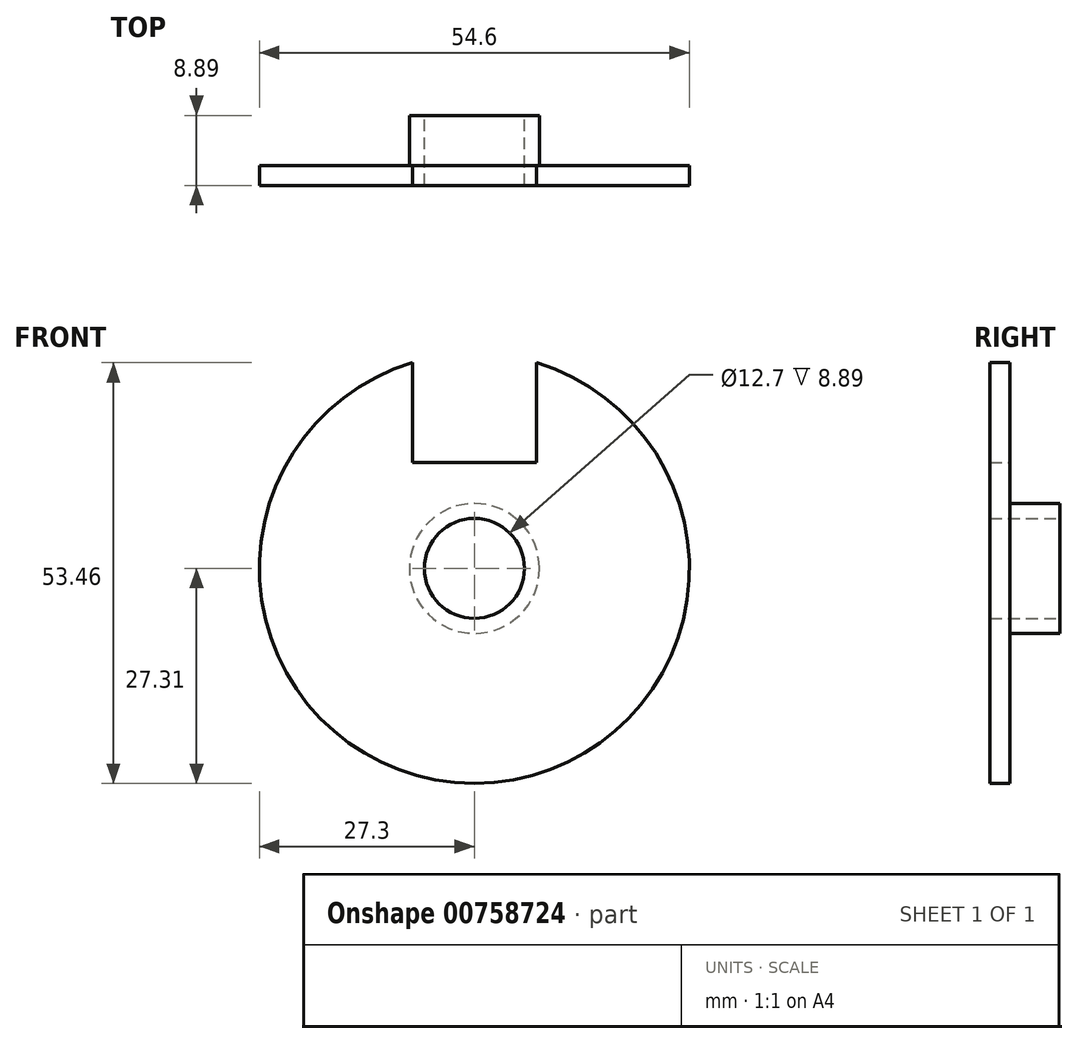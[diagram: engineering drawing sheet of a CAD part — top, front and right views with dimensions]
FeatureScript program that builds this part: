
annotation { "Feature Type Name" : "Feature", "Feature Type Description" : "" }
export const myFeature = defineFeature(function(context is Context, id is Id, definition is map)
    precondition{}
    {
        {
            var Q0;
            Q0=qCreatedBy(makeId("Front.planeOp"),FACE);
            var sketch = newSketch(context, id + "F0", { "sketchPlane" : qUnion([Q0])});
            skCircle(sketch, "E0", {"center": v(0, 0) * mm, "radius": 27.3 * mm});
            skCircle(sketch, "E1", {"center": v(0, 0) * mm, "radius": 6.35 * mm});
            skCircle(sketch, "E2", {"center": v(0, 0) * mm, "radius": 8.26 * mm});
            skLineSegment(sketch, "E3", {"start": v(0, 0) * mm, "end": v(0, 21.08) * mm});
            skCircle(sketch, "E4", {"center": v(0, 21.08) * mm, "radius": 7.62 * mm});
            skLineSegment(sketch, "E5", {"start": v(0, 21.08) * mm, "end": v(0, 13.46) * mm});
            skLineSegment(sketch, "E6", {"start": v(0, 13.46) * mm, "end": v(7.87, 13.46) * mm});
            skLineSegment(sketch, "E7", {"start": v(7.87, 13.46) * mm, "end": v(7.87, 29.17) * mm});
            skLineSegment(sketch, "E8", {"start": v(0, 13.46) * mm, "end": v(-7.87, 13.46) * mm});
            skLineSegment(sketch, "E9", {"start": v(-7.87, 13.46) * mm, "end": v(-7.87, 33.88) * mm});
            skSolve(sketch);
        }
        {
            var Q0;
            Q0=makeQuery(id+"F0.imprint","IMPRINT",FACE,{"disambiguationData":[TD([[makeQuery(id+"F0.imprint","IMPRINT",EDGE,{"derivedFrom":sQuery(id+"F0.wireOp",EDGE,"E2")}),-1.0]])]});
            var Q1;
            Q1=makeQuery(id+"F0.imprint","IMPRINT",FACE,{"disambiguationData":[TD([[makeQuery(id+"F0.imprint","IMPRINT",EDGE,{"derivedFrom":sQuery(id+"F0.wireOp",EDGE,"E1")}),-1.0]])]});
            extrude(context, id + "F1", {"entities" : qUnion([Q0, Q1]), "depth" : 2.54 * mm, "offsetDistance" : 25.4 * mm});
        }
        {
            var Q0;
            Q0=makeQuery(id+"F0.imprint","IMPRINT",FACE,{"disambiguationData":[TD([[makeQuery(id+"F0.imprint","IMPRINT",EDGE,{"derivedFrom":sQuery(id+"F0.wireOp",EDGE,"E1")}),-1.0]])]});
            extrude(context, id + "F2", {"entities" : qUnion([Q0]), "operationType" : NewBodyOperationType.ADD, "oppositeDirection" : true, "depth" : 6.35 * mm, "offsetDistance" : 25.4 * mm});
        }
    });
